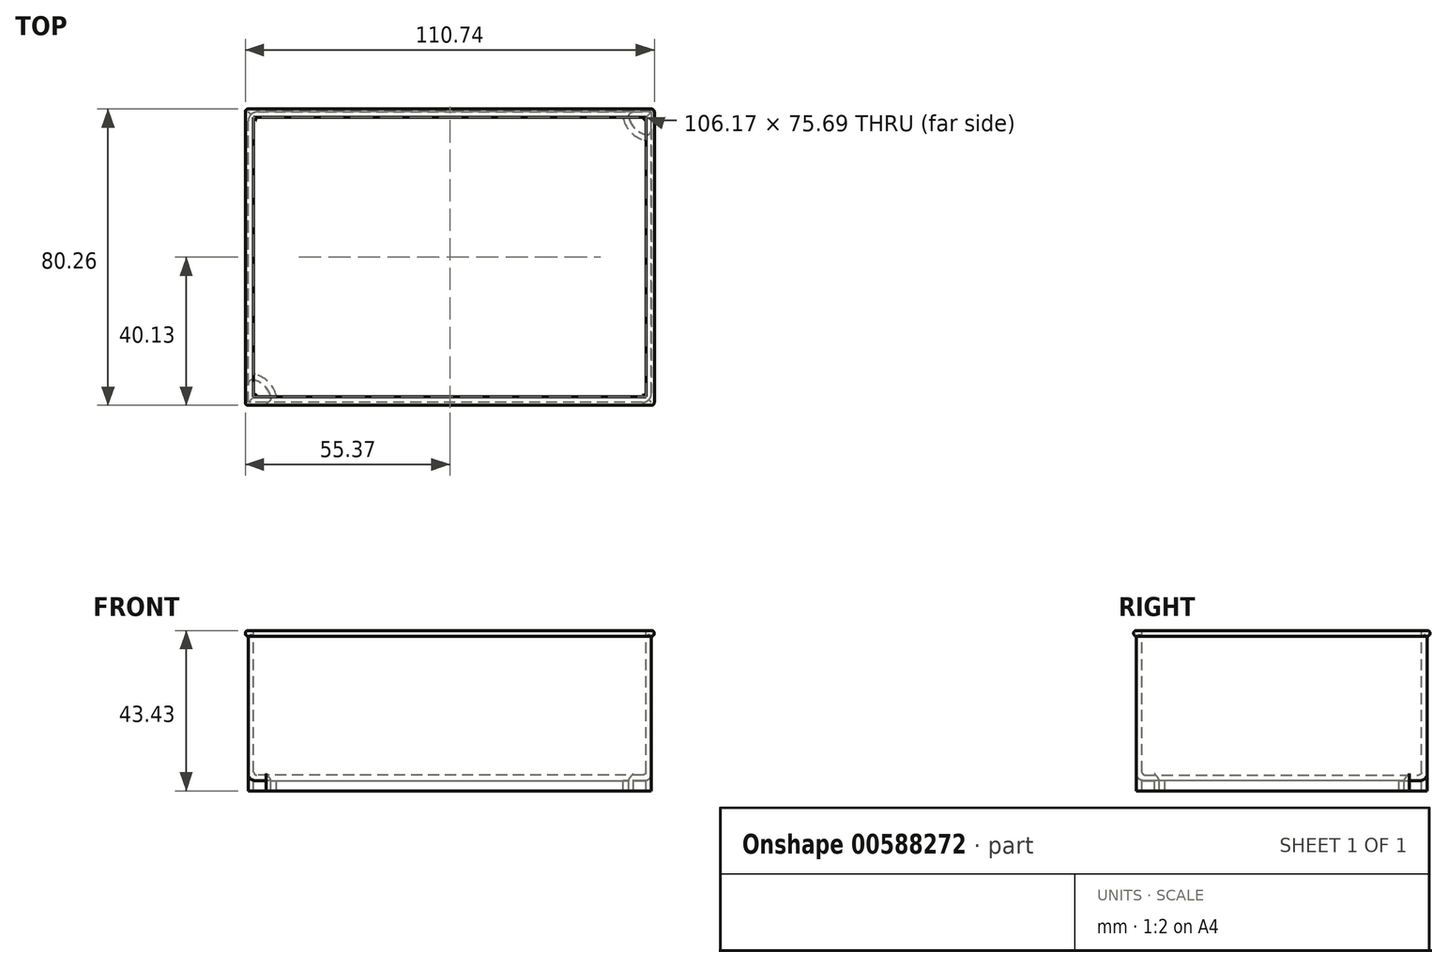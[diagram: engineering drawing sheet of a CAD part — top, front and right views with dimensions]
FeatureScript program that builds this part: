
annotation { "Feature Type Name" : "Feature", "Feature Type Description" : "" }
export const myFeature = defineFeature(function(context is Context, id is Id, definition is map)
    precondition{}
    {
        {
            var Q0;
            Q0=qCreatedBy(makeId("Front.planeOp"),FACE);
            var sketch = newSketch(context, id + "F0", { "sketchPlane" : qUnion([Q0])});
            skLineSegment(sketch, "E0.bottom", {"start": v(54.61, -20.32) * mm, "end": v(-54.61, -20.32) * mm});
            skLineSegment(sketch, "E0.top", {"start": v(54.61, 20.32) * mm, "end": v(-54.61, 20.32) * mm});
            skLineSegment(sketch, "E0.left", {"start": v(54.61, -20.32) * mm, "end": v(54.61, 20.32) * mm});
            skLineSegment(sketch, "E0.right", {"start": v(-54.61, -20.32) * mm, "end": v(-54.61, 20.32) * mm});
            skPoint(sketch, "E0.middle", {"position": v(0, 0) * mm});
            skSolve(sketch);
        }
        {
            var Q0;
            Q0=makeQuery(id+"F0.imprint","IMPRINT",FACE,{"disambiguationData":[TD([[makeQuery(id+"F0.imprint","IMPRINT",EDGE,{"derivedFrom":sQuery(id+"F0.wireOp",EDGE,"E0.bottom")}),-1.0]])]});
            extrude(context, id + "F1", {"entities" : qUnion([Q0]), "endBound" : BoundingType.SYMMETRIC, "depth" : 78.74 * mm});
        }
        {
            var Q0;
            Q0=makeQuery(id+"F1.opExtrude","SWEPT_FACE",FACE,{"disambiguationData":[OSD([sQuery(id+"F0.wireOp",EDGE,"E0.top")])]});
            shell(context, id + "F2", {"entities" : qUnion([Q0]), "thickness" : 1.52 * mm});
        }
        {
            var Q0;
            Q0=makeQuery(id+"F1.opExtrude","CAP_FACE",FACE,{"disambiguationData":[OSD([sQuery(id+"F0.wireOp",EDGE,"E0.bottom"),sQuery(id+"F0.wireOp",EDGE,"E0.top"),sQuery(id+"F0.wireOp",EDGE,"E0.left"),sQuery(id+"F0.wireOp",EDGE,"E0.right")])],"isStart":false});
            var sketch = newSketch(context, id + "F3", { "sketchPlane" : qUnion([Q0])});
            skArc(sketch, "E1", {"start": v(-54.61, 20.32) * mm, "mid": v(-55.37, 19.56) * mm, "end": v(-54.61, 18.8) * mm});
            skSolve(sketch);
        }
        {
            var Q0;
            {var subQ0=sQuery(id+"F3.wireOp",EDGE,"E1");Q0=makeQuery(id+"F3.imprint","IMPRINT",FACE,{"disambiguationData":[TD([[makeQuery(id+"F3.imprint","IMPRINT",EDGE,{"derivedFrom":subQ0}),1.0]])]});}
            var Q1;
            Q1=makeQuery(id+"F1.opExtrude","SWEPT_EDGE",EDGE,{"disambiguationData":[OSD([sQuery(id+"F0.wireOp",EDGE,"E0.top"),sQuery(id+"F0.wireOp",EDGE,"E0.right")])]});
            var Q2;
            Q2=makeQuery(id+"F1.opExtrude","CAP_EDGE",EDGE,{"disambiguationData":[OSD([sQuery(id+"F0.wireOp",EDGE,"E0.top")])],"isStart":true});
            var Q3;
            Q3=makeQuery(id+"F1.opExtrude","SWEPT_EDGE",EDGE,{"disambiguationData":[OSD([sQuery(id+"F0.wireOp",EDGE,"E0.top"),sQuery(id+"F0.wireOp",EDGE,"E0.left")])]});
            var Q4;
            Q4=makeQuery(id+"F1.opExtrude","CAP_EDGE",EDGE,{"disambiguationData":[OSD([sQuery(id+"F0.wireOp",EDGE,"E0.top")])],"isStart":false});
            sweep(context, id + "F4", {"operationType" : NewBodyOperationType.ADD, "profiles" : qUnion([Q0]), "path" : qUnion([Q1, Q2, Q3, Q4])});
        }
        {
            var Q0;
            Q0=makeQuery(id+"F1.opExtrude","SWEPT_FACE",FACE,{"disambiguationData":[OSD([sQuery(id+"F0.wireOp",EDGE,"E0.bottom")])]});
            var sketch = newSketch(context, id + "F5", { "sketchPlane" : qUnion([Q0])});
            skLineSegment(sketch, "E2.bottom", {"start": v(54.61, 39.37) * mm, "end": v(49.7, 39.37) * mm});
            skLineSegment(sketch, "E2.left", {"start": v(54.61, 39.37) * mm, "end": v(54.61, 34.45) * mm});
            skPoint(sketch, "E3.newPointA", {"position": v(48.26, 19.05) * mm});
            skArc(sketch, "E4", {"start": v(48.46, 37.78) * mm, "mid": v(50.12, 34.88) * mm, "end": v(53.02, 33.22) * mm});
            skPoint(sketch, "E5.visualSharp", {"position": v(48.26, 39.37) * mm});
            skArc(sketch, "E5.filletArc", {"start": v(49.7, 39.37) * mm, "mid": v(48.69, 38.88) * mm, "end": v(48.46, 37.78) * mm});
            skPoint(sketch, "E6.visualSharp", {"position": v(54.61, 33.02) * mm});
            skArc(sketch, "E6.filletArc", {"start": v(53.02, 33.22) * mm, "mid": v(54.12, 33.45) * mm, "end": v(54.6, 34.45) * mm});
            skArc(sketch, "E7.MirrorCS", {"start": v(-49.7, 39.37) * mm, "mid": v(-48.69, 38.88) * mm, "end": v(-48.46, 37.78) * mm});
            skArc(sketch, "E8.MirrorCS", {"start": v(-48.46, 37.78) * mm, "mid": v(-50.12, 34.88) * mm, "end": v(-53.02, 33.22) * mm});
            skArc(sketch, "E9.MirrorCS", {"start": v(-53.02, 33.22) * mm, "mid": v(-54.12, 33.45) * mm, "end": v(-54.6, 34.45) * mm});
            skLineSegment(sketch, "E10.MirrorCS", {"start": v(-54.61, 39.37) * mm, "end": v(-54.61, 34.45) * mm});
            skLineSegment(sketch, "E11.MirrorCS", {"start": v(-54.61, 39.37) * mm, "end": v(-49.7, 39.37) * mm});
            skArc(sketch, "E12.MirrorCS", {"start": v(-48.46, -37.78) * mm, "mid": v(-50.12, -34.88) * mm, "end": v(-53.02, -33.22) * mm});
            skArc(sketch, "E13.MirrorCS", {"start": v(-49.7, -39.37) * mm, "mid": v(-48.69, -38.88) * mm, "end": v(-48.46, -37.78) * mm});
            skLineSegment(sketch, "E14.MirrorCS", {"start": v(-54.6, -39.37) * mm, "end": v(-49.7, -39.37) * mm});
            skLineSegment(sketch, "E15.MirrorCS", {"start": v(-54.6, -39.37) * mm, "end": v(-54.6, -34.45) * mm});
            skArc(sketch, "E16.MirrorCS", {"start": v(-53.02, -33.22) * mm, "mid": v(-54.12, -33.45) * mm, "end": v(-54.6, -34.45) * mm});
            skArc(sketch, "E17.MirrorCS", {"start": v(49.7, -39.37) * mm, "mid": v(48.69, -38.88) * mm, "end": v(48.46, -37.78) * mm});
            skArc(sketch, "E18.MirrorCS", {"start": v(48.46, -37.78) * mm, "mid": v(50.12, -34.88) * mm, "end": v(53.02, -33.22) * mm});
            skArc(sketch, "E19.MirrorCS", {"start": v(53.02, -33.22) * mm, "mid": v(54.12, -33.45) * mm, "end": v(54.6, -34.45) * mm});
            skLineSegment(sketch, "E20.MirrorCS", {"start": v(54.6, -39.37) * mm, "end": v(54.6, -34.45) * mm});
            skLineSegment(sketch, "E21.MirrorCS", {"start": v(54.6, -39.37) * mm, "end": v(49.7, -39.37) * mm});
            skSolve(sketch);
        }
        {
            var Q0;
            Q0=makeQuery(id+"F5.imprint","IMPRINT",FACE,{"disambiguationData":[TD([[makeQuery(id+"F5.imprint","IMPRINT",EDGE,{"derivedFrom":sQuery(id+"F5.wireOp",EDGE,"E2.bottom")}),1.0]])]});
            var Q1;
            Q1=makeQuery(id+"F5.imprint","IMPRINT",FACE,{"disambiguationData":[TD([[makeQuery(id+"F5.imprint","IMPRINT",EDGE,{"derivedFrom":sQuery(id+"F5.wireOp",EDGE,"E8.MirrorCS")}),-1.0]])]});
            var Q2;
            Q2=makeQuery(id+"F5.imprint","IMPRINT",FACE,{"disambiguationData":[TD([[makeQuery(id+"F5.imprint","IMPRINT",EDGE,{"derivedFrom":sQuery(id+"F5.wireOp",EDGE,"E12.MirrorCS")}),1.0]])]});
            var Q3;
            Q3=makeQuery(id+"F5.imprint","IMPRINT",FACE,{"disambiguationData":[TD([[makeQuery(id+"F5.imprint","IMPRINT",EDGE,{"derivedFrom":sQuery(id+"F5.wireOp",EDGE,"E17.MirrorCS")}),-1.0]])]});
            extrude(context, id + "F6", {"entities" : qUnion([Q0, Q1, Q2, Q3]), "operationType" : NewBodyOperationType.ADD, "depth" : 2.8 * mm});
        }
        {
            var Q0;
            Q0=makeQuery(id+"F6.opExtrude","CAP_FACE",FACE,{"disambiguationData":[OSD([sQuery(id+"F5.wireOp",EDGE,"E2.bottom"),sQuery(id+"F5.wireOp",EDGE,"E2.left"),sQuery(id+"F5.wireOp",EDGE,"E4"),sQuery(id+"F5.wireOp",EDGE,"E5.filletArc"),sQuery(id+"F5.wireOp",EDGE,"E6.filletArc")])],"isStart":false});
            var Q1;
            Q1=makeQuery(id+"F6.opExtrude","CAP_FACE",FACE,{"disambiguationData":[OSD([sQuery(id+"F5.wireOp",EDGE,"E8.MirrorCS"),sQuery(id+"F5.wireOp",EDGE,"E9.MirrorCS"),sQuery(id+"F5.wireOp",EDGE,"E10.MirrorCS"),sQuery(id+"F5.wireOp",EDGE,"E7.MirrorCS"),sQuery(id+"F5.wireOp",EDGE,"E11.MirrorCS")])],"isStart":false});
            var Q2;
            Q2=makeQuery(id+"F6.opExtrude","CAP_FACE",FACE,{"disambiguationData":[OSD([sQuery(id+"F5.wireOp",EDGE,"E12.MirrorCS"),sQuery(id+"F5.wireOp",EDGE,"E13.MirrorCS"),sQuery(id+"F5.wireOp",EDGE,"E14.MirrorCS"),sQuery(id+"F5.wireOp",EDGE,"E15.MirrorCS"),sQuery(id+"F5.wireOp",EDGE,"E16.MirrorCS")])],"isStart":false});
            var Q3;
            Q3=makeQuery(id+"F6.opExtrude","CAP_FACE",FACE,{"disambiguationData":[OSD([sQuery(id+"F5.wireOp",EDGE,"E17.MirrorCS"),sQuery(id+"F5.wireOp",EDGE,"E18.MirrorCS"),sQuery(id+"F5.wireOp",EDGE,"E19.MirrorCS"),sQuery(id+"F5.wireOp",EDGE,"E20.MirrorCS"),sQuery(id+"F5.wireOp",EDGE,"E21.MirrorCS")])],"isStart":false});
            shell(context, id + "F7", {"entities" : qUnion([Q0, Q1, Q2, Q3]), "thickness" : 1.52 * mm});
        }
        {
            var Q0;
            Q0=makeQuery(id+"F2.opShell","OFFSET_FACE",FACE,{"disambiguationData":[OSD([sQuery(id+"F0.wireOp",EDGE,"E0.bottom")])]});
            fillet(context, id + "F8", {"entities" : qUnion([Q0]), "radius" : 0.76 * mm, "tangentPropagation" : true, "allowEdgeOverflow" : false});
        }
        {
            var Q0;
            Q0=makeQuery(id+"F1.opExtrude","SWEPT_EDGE",EDGE,{"disambiguationData":[OSD([sQuery(id+"F0.wireOp",EDGE,"E0.bottom"),sQuery(id+"F0.wireOp",EDGE,"E0.right")])]});
            var Q1;
            Q1=makeQuery(id+"F1.opExtrude","CAP_EDGE",EDGE,{"disambiguationData":[OSD([sQuery(id+"F0.wireOp",EDGE,"E0.bottom")])],"isStart":false});
            var Q2;
            Q2=makeQuery(id+"F1.opExtrude","SWEPT_EDGE",EDGE,{"disambiguationData":[OSD([sQuery(id+"F0.wireOp",EDGE,"E0.bottom"),sQuery(id+"F0.wireOp",EDGE,"E0.left")])]});
            var Q3;
            Q3=makeQuery(id+"F1.opExtrude","CAP_EDGE",EDGE,{"disambiguationData":[OSD([sQuery(id+"F0.wireOp",EDGE,"E0.bottom")])],"isStart":true});
            fillet(context, id + "F9", {"entities" : qUnion([Q0, Q1, Q2, Q3]), "radius" : 1.9 * mm, "tangentPropagation" : true, "allowEdgeOverflow" : false});
        }
        {
            var Q0;
            Q0=makeQuery(id+"F4.opSweep","MID_CAP_EDGE",EDGE,{"disambiguationData":[OSD([sQuery(id+"F0.wireOp",EDGE,"E0.top"),sQuery(id+"F0.wireOp",EDGE,"E0.left"),sQuery(id+"F3.wireOp",EDGE,"E1")])],"capPos":3.0});
            var Q1;
            Q1=makeQuery(id+"F4.opSweep","MID_CAP_EDGE",EDGE,{"disambiguationData":[OSD([sQuery(id+"F0.wireOp",EDGE,"E0.top"),sQuery(id+"F0.wireOp",EDGE,"E0.left"),sQuery(id+"F3.wireOp",EDGE,"E1")])],"capPos":2.0});
            var Q2;
            Q2=makeQuery(id+"F4.opSweep","MID_CAP_EDGE",EDGE,{"disambiguationData":[OSD([sQuery(id+"F0.wireOp",EDGE,"E0.top"),sQuery(id+"F0.wireOp",EDGE,"E0.right"),sQuery(id+"F3.wireOp",EDGE,"E1")])],"capPos":1.0});
            var Q3;
            Q3=makeQuery(id+"F4.opSweep","CAP_EDGE",EDGE,{"disambiguationData":[OSD([sQuery(id+"F0.wireOp",EDGE,"E0.top"),sQuery(id+"F0.wireOp",EDGE,"E0.right"),sQuery(id+"F3.wireOp",EDGE,"E1")])],"isStart":true});
            fillet(context, id + "F10", {"entities" : qUnion([Q0, Q1, Q2, Q3]), "radius" : 0.76 * mm, "tangentPropagation" : true, "allowEdgeOverflow" : false});
        }
        {
            var Q0;
            Q0=makeQuery(id+"F6.boolean.opBoolean","MERGE",EDGE,{"derivedFrom":[makeQuery(id+"F1.opExtrude","CAP_EDGE",EDGE,{"disambiguationData":[OSD([sQuery(id+"F0.wireOp",EDGE,"E0.left")])],"isStart":false}),makeQuery(id+"F6.opExtrude","SWEPT_EDGE",EDGE,{"disambiguationData":[OSD([sQuery(id+"F5.wireOp",EDGE,"E2.bottom"),sQuery(id+"F5.wireOp",EDGE,"E2.left")])]})]});
            var Q1;
            Q1=makeQuery(id+"F6.boolean.opBoolean","MERGE",EDGE,{"derivedFrom":[makeQuery(id+"F1.opExtrude","CAP_EDGE",EDGE,{"disambiguationData":[OSD([sQuery(id+"F0.wireOp",EDGE,"E0.left")])],"isStart":true}),makeQuery(id+"F6.opExtrude","SWEPT_EDGE",EDGE,{"disambiguationData":[OSD([sQuery(id+"F5.wireOp",EDGE,"E20.MirrorCS"),sQuery(id+"F5.wireOp",EDGE,"E21.MirrorCS")])]})]});
            var Q2;
            Q2=makeQuery(id+"F6.boolean.opBoolean","MERGE",EDGE,{"derivedFrom":[makeQuery(id+"F1.opExtrude","CAP_EDGE",EDGE,{"disambiguationData":[OSD([sQuery(id+"F0.wireOp",EDGE,"E0.right")])],"isStart":false}),makeQuery(id+"F6.opExtrude","SWEPT_EDGE",EDGE,{"disambiguationData":[OSD([sQuery(id+"F5.wireOp",EDGE,"E10.MirrorCS"),sQuery(id+"F5.wireOp",EDGE,"E11.MirrorCS")])]})]});
            var Q3;
            Q3=makeQuery(id+"F6.boolean.opBoolean","MERGE",EDGE,{"derivedFrom":[makeQuery(id+"F1.opExtrude","CAP_EDGE",EDGE,{"disambiguationData":[OSD([sQuery(id+"F0.wireOp",EDGE,"E0.right")])],"isStart":true}),makeQuery(id+"F6.opExtrude","SWEPT_EDGE",EDGE,{"disambiguationData":[OSD([sQuery(id+"F5.wireOp",EDGE,"E14.MirrorCS"),sQuery(id+"F5.wireOp",EDGE,"E15.MirrorCS")])]})]});
            fillet(context, id + "F11", {"entities" : qUnion([Q0, Q1, Q2, Q3]), "radius" : 2.54 * mm, "tangentPropagation" : true, "allowEdgeOverflow" : false});
        }
    });
